# Revit family: LTDCR-LRC-2X2
name_source: partatom
category: Lighting Fixtures
units: mm (PartAtom-declared; Revit-internal decimal feet)

## family parameters
Always vertical = Yes
Cut with Voids When Loaded = No
Host = Ceiling
Light Source = Yes
OmniClass Number = 23.80.70.11
OmniClass Title = Luminaries for Internal Lighting
Part Type = Normal
Room Calculation Point = No
Round Connector Dimension = Use Diameter
Shared = No

## types (3) — shared parameters
Assembly Code = D5020200
Color Filter = 16777215
Description = LED Circular Recessed Luminaire with Ligature Resistant Construction
Dimming Lamp Color Temperature Shift = <None>
Emit Shape Visible in Rendering = No
Emit from Rectangle Length = 1' - 10 3/4"
Emit from Rectangle Width = 1' - 10 3/4"
Housing Finish = Metal - Viscor - White
Lamp = LED
Length = 1' - 10 3/4"
Lens Finish = Polycarbonate - Viscor - Frosted Round
Manufacturer = CERTOLUX A DIVISION OF VISCOR
Model = LTDCR-LRC
Tilt Angle = 90.00°
URL = https://www.viscor.com
Voltage = 120 V
Width = 1' - 10 3/4"

## per-type parameters (varying)
| type | Apparent Load | Lamp Wattage | Photometric Web File |
| LTDCR-LRC 2X2-LED840K022L-C87-P08_P73 | 22 VA | 22 VA | LTDCR-LRC 2X2-LED840K022L-C87-P08_P73.ies |
| LTDCR-LRC 2X2-LED840K035L-C87-P08_P73 | 35 VA | 35 VA | LTDCR-LRC 2X2-LED840K035L-C87-P08_P73.ies |
| LTDCR-LRC 2X2-LED840K050L-C87-P08_P73 | 51 VA | 51 VA | LTDCR-LRC 2X2-LED840K050L-C87-P08_P73.ies |

## geometry (parser evidence)
native form markers: Sweep x3
no freeform markers — native parametric forms only
